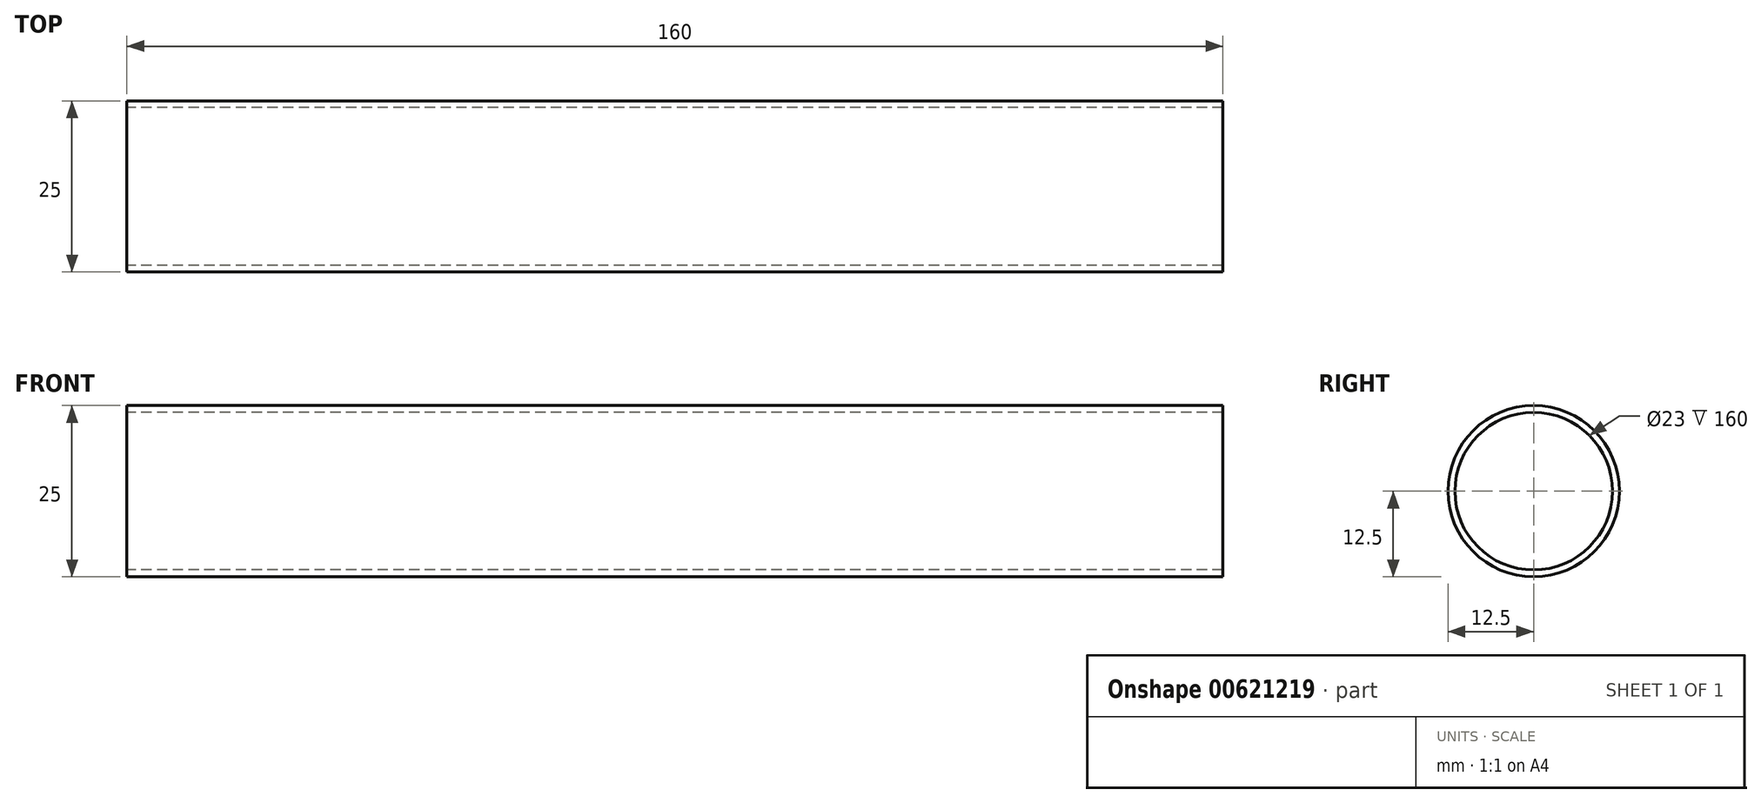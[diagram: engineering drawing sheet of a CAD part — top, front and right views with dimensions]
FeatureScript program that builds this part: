
annotation { "Feature Type Name" : "Feature", "Feature Type Description" : "" }
export const myFeature = defineFeature(function(context is Context, id is Id, definition is map)
    precondition{}
    {
        {
            var Q0;
            Q0=qCreatedBy(makeId("Right.planeOp"),FACE);
            var sketch = newSketch(context, id + "F0", { "sketchPlane" : qUnion([Q0])});
            skCircle(sketch, "E0", {"center": v(0, 0) * mm, "radius": 12.5 * mm});
            skCircle(sketch, "E1", {"center": v(0, 0) * mm, "radius": 11.5 * mm});
            skSolve(sketch);
        }
        {
            var Q0;
            Q0 = qSketchRegion(id + "F0", true);
            extrude(context, id + "F1", {"entities" : qUnion([Q0]), "depth" : 160 * mm, "offsetDistance" : 25 * mm});
        }
    });
